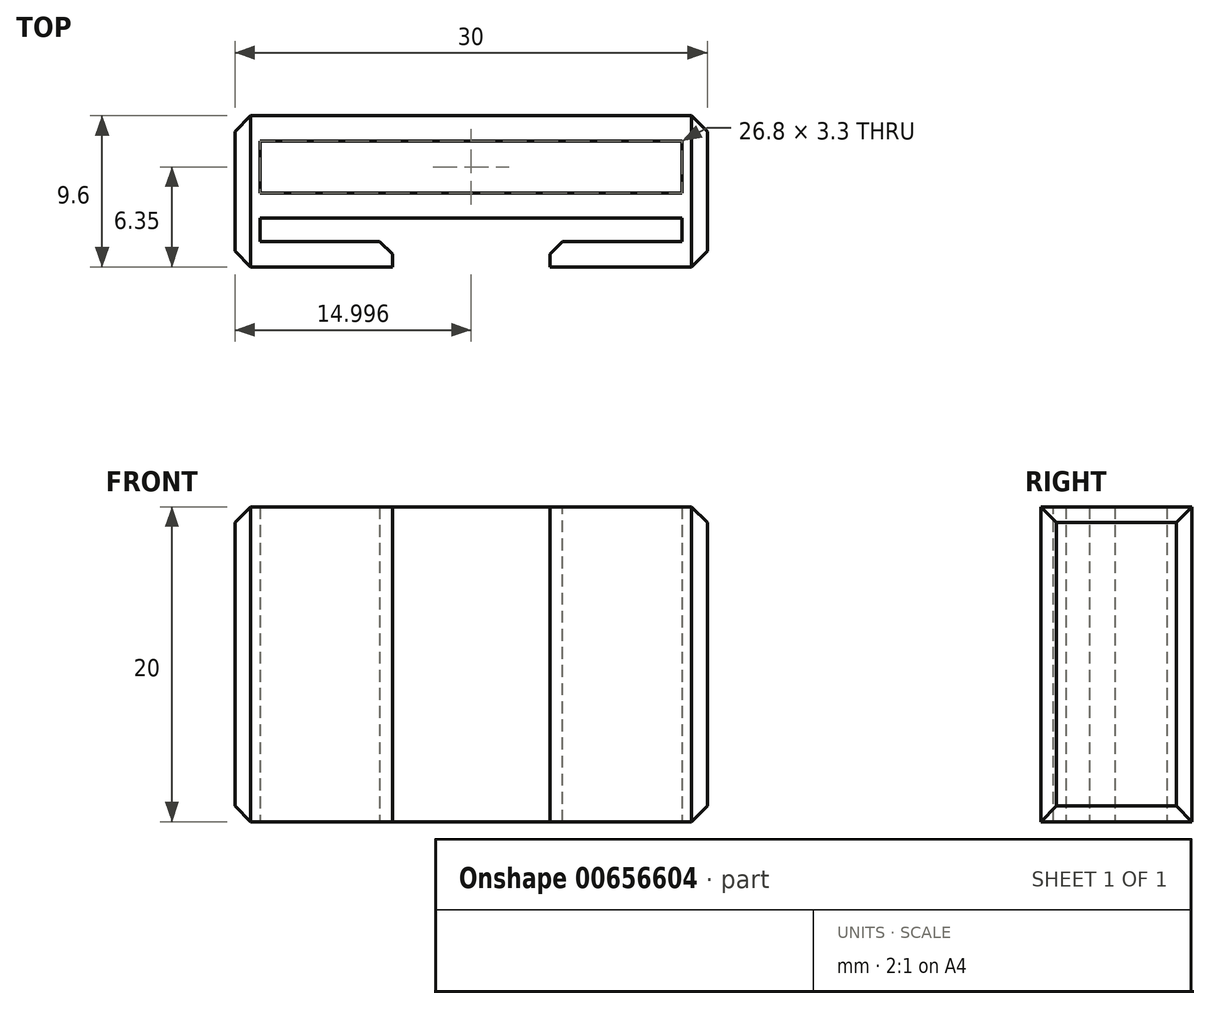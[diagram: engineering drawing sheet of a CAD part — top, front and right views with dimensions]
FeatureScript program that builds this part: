
annotation { "Feature Type Name" : "Feature", "Feature Type Description" : "" }
export const myFeature = defineFeature(function(context is Context, id is Id, definition is map)
    precondition{}
    {
        {
            var Q0;
            Q0=qCreatedBy(makeId("Top.planeOp"),FACE);
            var sketch = newSketch(context, id + "F0", { "sketchPlane" : qUnion([Q0])});
            skLineSegment(sketch, "E0", {"start": v(-15, 0) * mm, "end": v(15, 0) * mm});
            skLineSegment(sketch, "E1", {"start": v(15, 0) * mm, "end": v(15, -4.7) * mm});
            skLineSegment(sketch, "E2", {"start": v(15, -4.7) * mm, "end": v(5, -4.7) * mm});
            skLineSegment(sketch, "E3", {"start": v(5, -4.7) * mm, "end": v(5, -3.1) * mm});
            skLineSegment(sketch, "E4", {"start": v(5, -3.1) * mm, "end": v(13.4, -3.1) * mm});
            skLineSegment(sketch, "E5", {"start": v(13.4, -3.1) * mm, "end": v(13.4, -1.6) * mm});
            skLineSegment(sketch, "E6", {"start": v(13.4, -1.6) * mm, "end": v(13.4, -1.6) * mm});
            skLineSegment(sketch, "E7", {"start": v(-15, 0) * mm, "end": v(-15, -4.7) * mm});
            skLineSegment(sketch, "E8", {"start": v(-15, -4.7) * mm, "end": v(-5, -4.7) * mm});
            skLineSegment(sketch, "E9", {"start": v(-5, -4.7) * mm, "end": v(-5, -3.1) * mm});
            skLineSegment(sketch, "E10", {"start": v(-5, -3.1) * mm, "end": v(-13.4, -3.1) * mm});
            skLineSegment(sketch, "E11", {"start": v(-13.4, -3.1) * mm, "end": v(-13.4, -1.6) * mm});
            skLineSegment(sketch, "E12", {"start": v(13.4, -1.6) * mm, "end": v(-13.4, -1.6) * mm});
            skLineSegment(sketch, "E13", {"start": v(15, 0) * mm, "end": v(15, 4.9) * mm});
            skLineSegment(sketch, "E14", {"start": v(15, 4.9) * mm, "end": v(-15, 4.9) * mm});
            skLineSegment(sketch, "E15", {"start": v(-15, 4.9) * mm, "end": v(-15, 0) * mm});
            skLineSegment(sketch, "E16", {"start": v(-13.4, 0) * mm, "end": v(-13.4, 3.3) * mm});
            skLineSegment(sketch, "E17", {"start": v(-13.4, 3.3) * mm, "end": v(13.4, 3.3) * mm});
            skLineSegment(sketch, "E18", {"start": v(13.4, 3.3) * mm, "end": v(13.4, 0) * mm});
            skLineSegment(sketch, "E19", {"start": v(13.4, 0) * mm, "end": v(-13.4, 0) * mm});
            skSolve(sketch);
        }
        {
            var Q0;
            {var subQ0=sQuery(id+"F0.wireOp",EDGE,"E13");Q0=makeQuery(id+"F0.imprint","IMPRINT",FACE,{"disambiguationData":[TD([[makeQuery(id+"F0.imprint","IMPRINT",EDGE,{"derivedFrom":subQ0}),1.0]])]});}
            var Q1;
            {var subQ3=sQuery(id+"F0.wireOp",EDGE,"E1");Q1=makeQuery(id+"F0.imprint","IMPRINT",FACE,{"disambiguationData":[TD([[makeQuery(id+"F0.imprint","IMPRINT",EDGE,{"derivedFrom":subQ3}),-1.0]])]});}
            extrude(context, id + "F1", {"entities" : qUnion([Q0, Q1]), "depth" : 20 * mm, "offsetDistance" : 25 * mm});
        }
        {
            var Q0;
            Q0=makeQuery(id+"F1.opExtrude","SWEPT_EDGE",EDGE,{"disambiguationData":[OSD([sQuery(id+"F0.wireOp",EDGE,"E9"),sQuery(id+"F0.wireOp",EDGE,"E10")])]});
            var Q1;
            Q1=makeQuery(id+"F1.opExtrude","SWEPT_EDGE",EDGE,{"disambiguationData":[OSD([sQuery(id+"F0.wireOp",EDGE,"E3"),sQuery(id+"F0.wireOp",EDGE,"E4")])]});
            chamfer(context, id + "F2", {"entities" : qUnion([Q0, Q1]), "width" : 0.8 * mm, "tangentPropagation" : true});
        }
        {
            var Q0;
            Q0=makeQuery(id+"F1.opExtrude","SWEPT_FACE",FACE,{"disambiguationData":[OSD([sQuery(id+"F0.wireOp",EDGE,"E7"),sQuery(id+"F0.wireOp",EDGE,"E15")])]});
            var Q1;
            Q1=makeQuery(id+"F1.opExtrude","SWEPT_FACE",FACE,{"disambiguationData":[OSD([sQuery(id+"F0.wireOp",EDGE,"E1"),sQuery(id+"F0.wireOp",EDGE,"E13")])]});
            chamfer(context, id + "F3", {"entities" : qUnion([Q0, Q1]), "width" : 1 * mm, "tangentPropagation" : true});
        }
    });
